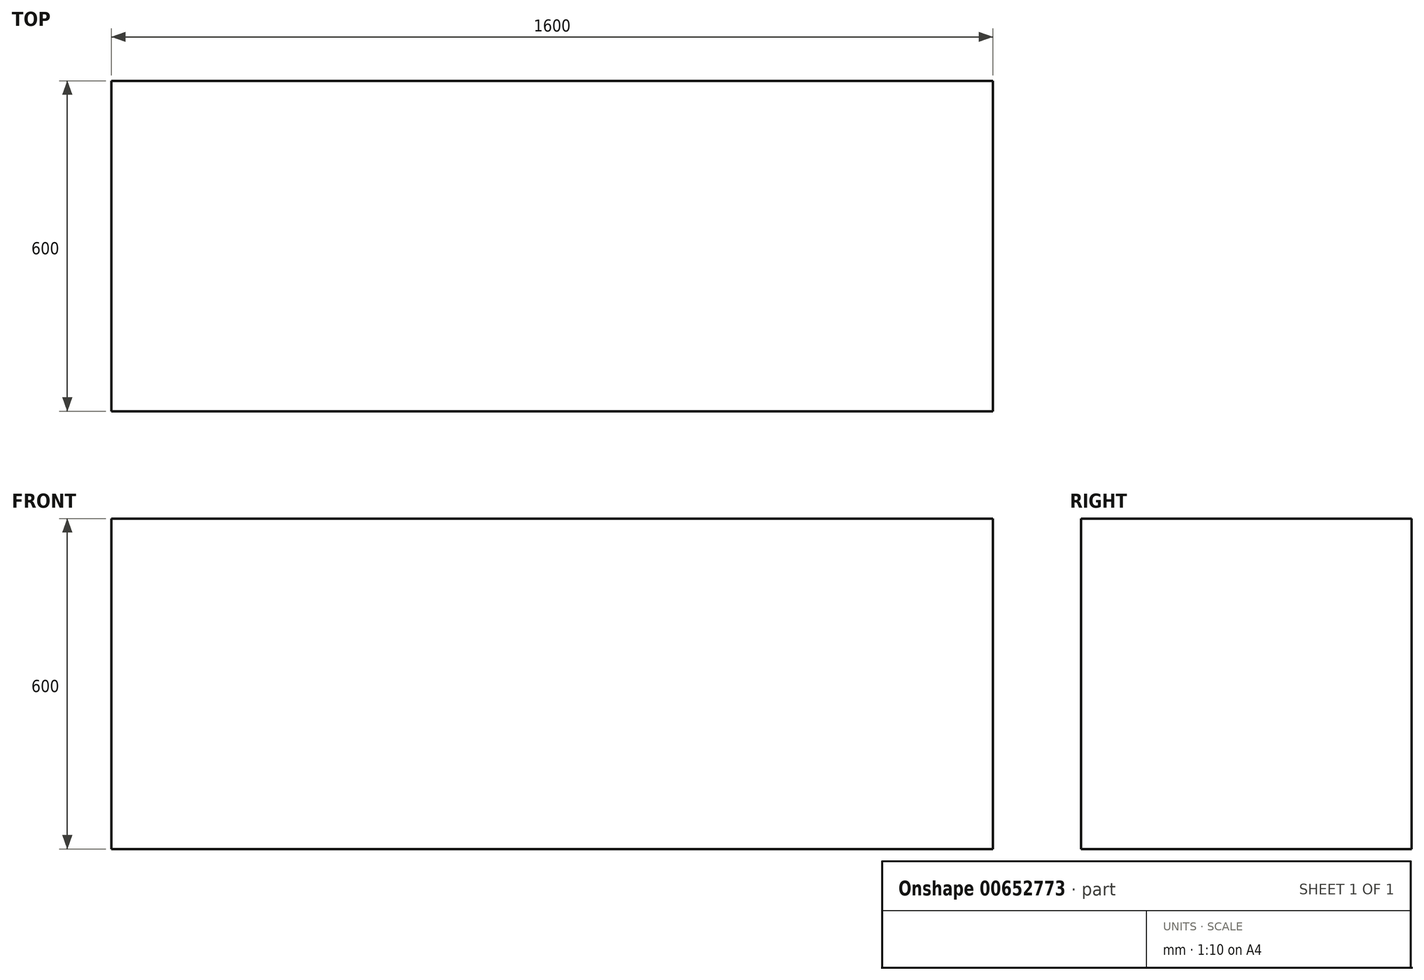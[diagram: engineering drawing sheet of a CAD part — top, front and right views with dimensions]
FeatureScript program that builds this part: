
annotation { "Feature Type Name" : "Feature", "Feature Type Description" : "" }
export const myFeature = defineFeature(function(context is Context, id is Id, definition is map)
    precondition{}
    {
        {
            var Q0;
            Q0=qCreatedBy(makeId("Front.planeOp"),FACE);
            var sketch = newSketch(context, id + "F0", { "sketchPlane" : qUnion([Q0])});
            skLineSegment(sketch, "E0.bottom", {"start": v(800, 300) * mm, "end": v(-800, 300) * mm});
            skLineSegment(sketch, "E0.top", {"start": v(800, -300) * mm, "end": v(-800, -300) * mm});
            skLineSegment(sketch, "E0.left", {"start": v(800, 300) * mm, "end": v(800, -300) * mm});
            skLineSegment(sketch, "E0.right", {"start": v(-800, 300) * mm, "end": v(-800, -300) * mm});
            skPoint(sketch, "E0.middle", {"position": v(0, 0) * mm});
            skSolve(sketch);
        }
        {
            var Q0;
            Q0=makeQuery(id+"F0.imprint","IMPRINT",FACE,{"disambiguationData":[TD([[makeQuery(id+"F0.imprint","IMPRINT",EDGE,{"derivedFrom":sQuery(id+"F0.wireOp",EDGE,"E0.bottom")}),1.0]])]});
            extrude(context, id + "F1", {"entities" : qUnion([Q0]), "depth" : 600 * mm, "offsetDistance" : 25 * mm});
        }
    });
